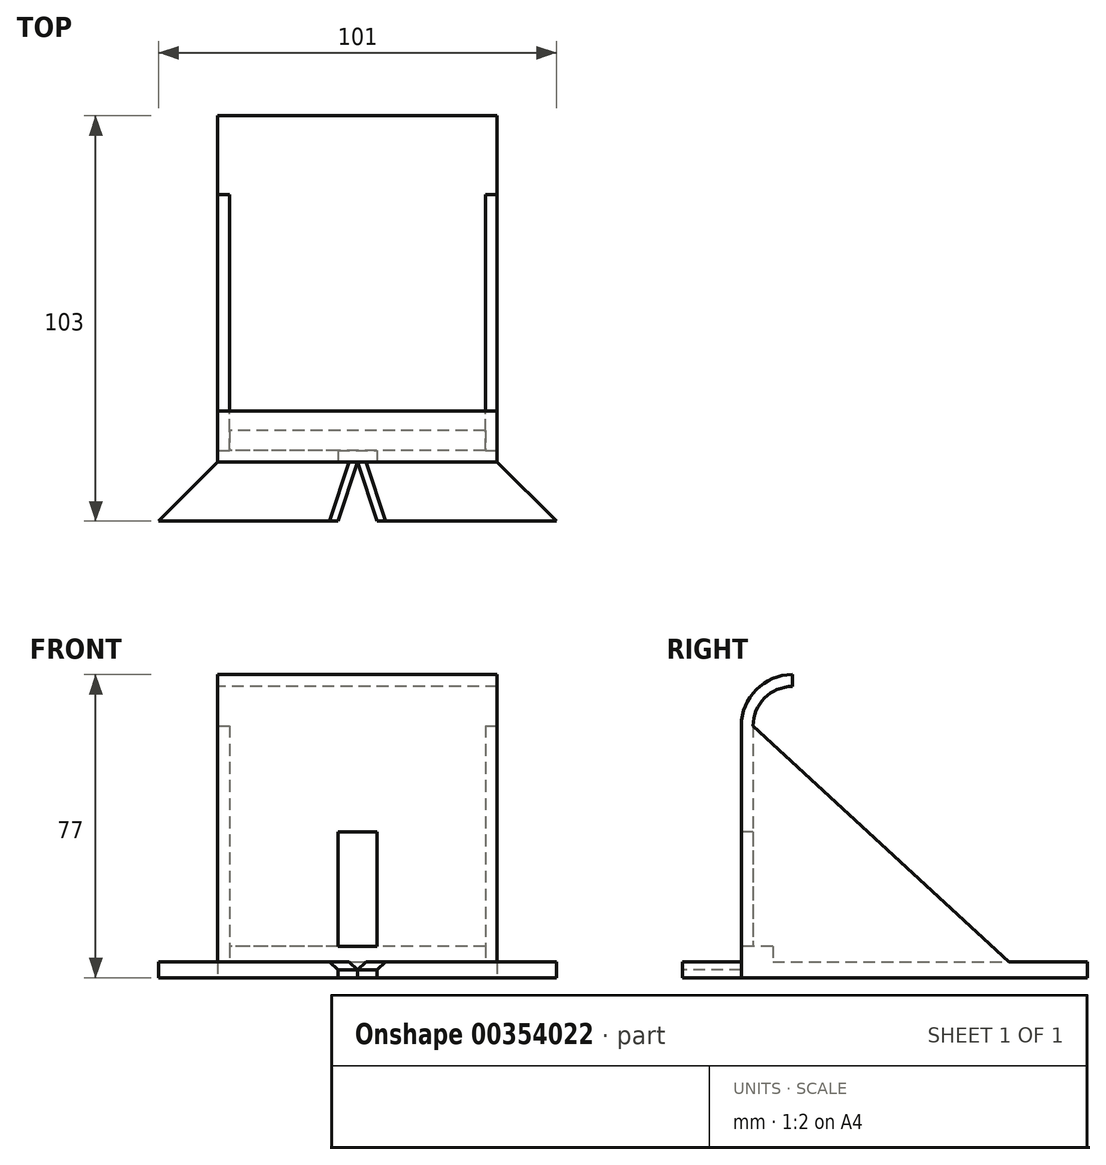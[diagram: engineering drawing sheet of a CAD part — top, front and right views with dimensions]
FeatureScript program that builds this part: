
annotation { "Feature Type Name" : "Feature", "Feature Type Description" : "" }
export const myFeature = defineFeature(function(context is Context, id is Id, definition is map)
    precondition{}
    {
        {
            var Q0;
            Q0=qCreatedBy(makeId("Top.planeOp"),FACE);
            var sketch = newSketch(context, id + "F0", { "sketchPlane" : qUnion([Q0])});
            skLineSegment(sketch, "E0.bottom", {"start": v(-32.5, -32.5) * mm, "end": v(32.5, -32.5) * mm});
            skLineSegment(sketch, "E0.top", {"start": v(-32.5, 32.5) * mm, "end": v(32.5, 32.5) * mm});
            skLineSegment(sketch, "E0.left", {"start": v(-32.5, -32.5) * mm, "end": v(-32.5, 32.5) * mm});
            skLineSegment(sketch, "E0.right", {"start": v(32.5, -32.5) * mm, "end": v(32.5, 32.5) * mm});
            skPoint(sketch, "E0.middle", {"position": v(0, 0) * mm});
            skLineSegment(sketch, "E1.0", {"start": v(35.5, -35.5) * mm, "end": v(35.5, 32.5) * mm});
            skLineSegment(sketch, "E1.1", {"start": v(-35.5, -35.5) * mm, "end": v(35.5, -35.5) * mm});
            skLineSegment(sketch, "E1.2", {"start": v(-35.5, -35.5) * mm, "end": v(-35.5, 32.5) * mm});
            skLineSegment(sketch, "E2", {"start": v(-32.5, 32.5) * mm, "end": v(-35.5, 32.5) * mm});
            skLineSegment(sketch, "E3", {"start": v(32.5, 32.5) * mm, "end": v(35.5, 32.5) * mm});
            skLineSegment(sketch, "E4", {"start": v(35.5, -35.5) * mm, "end": v(35.5, -50.5) * mm});
            skLineSegment(sketch, "E5", {"start": v(-35.5, -50.5) * mm, "end": v(-35.5, -35.5) * mm});
            skLineSegment(sketch, "E6", {"start": v(35.5, -35.5) * mm, "end": v(50.5, -50.5) * mm});
            skLineSegment(sketch, "E7.MirrorCS", {"start": v(-35.5, -35.5) * mm, "end": v(-50.5, -50.5) * mm});
            skLineSegment(sketch, "E8", {"start": v(5.98, -50.5) * mm, "end": v(5, -50.5) * mm});
            skLineSegment(sketch, "E9", {"start": v(5.98, -50.5) * mm, "end": v(50.5, -50.5) * mm});
            skLineSegment(sketch, "E10", {"start": v(5, -50.5) * mm, "end": v(0, -35.5) * mm});
            skLineSegment(sketch, "E11.MirrorCS", {"start": v(-5, -50.5) * mm, "end": v(0, -35.5) * mm});
            skLineSegment(sketch, "E12.trimOffspring", {"start": v(-5, -50.5) * mm, "end": v(-50.5, -50.5) * mm});
            skSolve(sketch);
        }
        {
            var Q0;
            Q0 = qSketchRegion(id + "F0", true);
            extrude(context, id + "F1", {"entities" : qUnion([Q0]), "depth" : 4 * mm});
        }
        {
            var Q0;
            Q0=makeQuery(id+"F1.opExtrude","CAP_FACE",FACE,{"disambiguationData":[OSD([sQuery(id+"F0.wireOp",EDGE,"E0.top"),sQuery(id+"F0.wireOp",EDGE,"E1.0"),sQuery(id+"F0.wireOp",EDGE,"E1.1"),sQuery(id+"F0.wireOp",EDGE,"E1.2"),sQuery(id+"F0.wireOp",EDGE,"E2"),sQuery(id+"F0.wireOp",EDGE,"E3")])],"isStart":false});
            var sketch = newSketch(context, id + "F2", { "sketchPlane" : qUnion([Q0])});
            skLineSegment(sketch, "E13.0", {"start": v(-32.5, -32.5) * mm, "end": v(32.5, -32.5) * mm});
            skLineSegment(sketch, "E14.0", {"start": v(-32.5, -32.5) * mm, "end": v(-32.5, 32.5) * mm});
            skLineSegment(sketch, "E15.0", {"start": v(32.5, -32.5) * mm, "end": v(32.5, 32.5) * mm});
            skLineSegment(sketch, "E16", {"start": v(-35.5, -35.5) * mm, "end": v(35.5, -35.5) * mm});
            skSolve(sketch);
        }
        {
            var Q0;
            Q0 = qSketchRegion(id + "F2", true);
            var Q1;
            Q1=makeQuery(id+"F2.imprint","IMPRINT",FACE,{"disambiguationData":[TD([[makeQuery(id+"F2.imprint","IMPRINT",EDGE,{"derivedFrom":sQuery(id+"F2.wireOp",EDGE,"E13.0")}),-1.0]])]});
            extrude(context, id + "F3", {"entities" : qUnion([Q0, Q1]), "operationType" : NewBodyOperationType.ADD, "depth" : 60 * mm});
        }
        {
            var Q0;
            {var subQ0=sQuery(id+"F0.wireOp",EDGE,"E1.0");Q0=makeQuery(id+"F3.boolean.opBoolean","MERGE",FACE,{"derivedFrom":[makeQuery(id+"F1.opExtrude","SWEPT_FACE",FACE,{"disambiguationData":[OSD([subQ0])]}),makeQuery(id+"F3.opExtrude","SWEPT_FACE",FACE,{"disambiguationData":[OSD([subQ0])]})]});}
            var sketch = newSketch(context, id + "F4", { "sketchPlane" : qUnion([Q0])});
            skLineSegment(sketch, "E17", {"start": v(32.5, 4) * mm, "end": v(-32.5, 64) * mm});
            skLineSegment(sketch, "E18.0.0", {"start": v(-35.5, 0) * mm, "end": v(32.5, 0) * mm});
            skLineSegment(sketch, "E18.0.1", {"start": v(32.5, 0) * mm, "end": v(32.5, 64) * mm});
            skLineSegment(sketch, "E18.0.2", {"start": v(32.5, 64) * mm, "end": v(-35.5, 64) * mm});
            skLineSegment(sketch, "E18.0.3", {"start": v(-35.5, 64) * mm, "end": v(-35.5, 0) * mm});
            skSolve(sketch);
        }
        {
            var Q0;
            {var subQ0=sQuery(id+"F4.wireOp",EDGE,"E17");Q0=makeQuery(id+"F4.imprint","IMPRINT",FACE,{"disambiguationData":[TD([[makeQuery(id+"F4.imprint","IMPRINT",EDGE,{"derivedFrom":subQ0}),-1.0]])]});}
            extrude(context, id + "F5", {"entities" : qUnion([Q0]), "operationType" : NewBodyOperationType.REMOVE, "oppositeDirection" : true, "depth" : 105.7 * mm});
        }
        {
            var Q0;
            Q0=makeQuery(id+"F3.opExtrude","SWEPT_FACE",FACE,{"disambiguationData":[OSD([sQuery(id+"F2.wireOp",EDGE,"E16")])]});
            var sketch = newSketch(context, id + "F6", { "sketchPlane" : qUnion([Q0])});
            skLineSegment(sketch, "E19", {"start": v(0, 8) * mm, "end": v(25, 8) * mm});
            skLineSegment(sketch, "E20", {"start": v(25, 8) * mm, "end": v(-25, 8) * mm});
            skLineSegment(sketch, "E21", {"start": v(-25, 8) * mm, "end": v(-25, 19) * mm});
            skLineSegment(sketch, "E22", {"start": v(0, 8) * mm, "end": v(3.48, 8) * mm});
            skLineSegment(sketch, "E23", {"start": v(0, 8) * mm, "end": v(-5, 8) * mm});
            skLineSegment(sketch, "E24", {"start": v(-5, 19) * mm, "end": v(-5, 37) * mm});
            skLineSegment(sketch, "E25", {"start": v(-25, 19) * mm, "end": v(-5, 19) * mm});
            skLineSegment(sketch, "E26", {"start": v(-5, 37) * mm, "end": v(0, 37) * mm});
            skPoint(sketch, "E26.endSnap0", {"position": v(0, 6) * mm});
            skLineSegment(sketch, "E27.MirrorCS", {"start": v(5, 19) * mm, "end": v(5, 37) * mm});
            skLineSegment(sketch, "E28.MirrorCS", {"start": v(5, 37) * mm, "end": v(0, 37) * mm});
            skLineSegment(sketch, "E29.MirrorCS", {"start": v(25, 19) * mm, "end": v(5, 19) * mm});
            skLineSegment(sketch, "E30.MirrorCS", {"start": v(25, 8) * mm, "end": v(25, 19) * mm});
            skPoint(sketch, "E31.orphan", {"position": v(5, 8) * mm});
            skSolve(sketch);
        }
        {
            var Q0;
            Q0 = qSketchRegion(id + "F6", true);
            extrude(context, id + "F7", {"entities" : qUnion([Q0]), "operationType" : NewBodyOperationType.REMOVE, "oppositeDirection" : true, "depth" : 25 * mm});
        }
        {
            var Q0;
            Q0=makeQuery(id+"F1.opExtrude","CAP_EDGE",EDGE,{"disambiguationData":[OSD([sQuery(id+"F0.wireOp",EDGE,"E11.MirrorCS")])],"isStart":false});
            chamfer(context, id + "F8", {"entities" : qUnion([Q0]), "width" : 2 * mm, "tangentPropagation" : true});
        }
        {
            var Q0;
            Q0=makeQuery(id+"F1.opExtrude","CAP_EDGE",EDGE,{"disambiguationData":[OSD([sQuery(id+"F0.wireOp",EDGE,"E10")])],"isStart":false});
            chamfer(context, id + "F9", {"entities" : qUnion([Q0]), "width" : 2 * mm, "tangentPropagation" : true});
        }
        {
            var Q0;
            {var subQ0=sQuery(id+"F0.wireOp",EDGE,"E3");var subQ1=sQuery(id+"F0.wireOp",EDGE,"E2");var subQ2=sQuery(id+"F0.wireOp",EDGE,"E0.top");var subQ3=makeQuery(id+"F1.opExtrude","CAP_EDGE",EDGE,{"disambiguationData":[OSD([subQ2,subQ1,subQ0])],"isStart":false});Q0=makeQuery(id+"F3.boolean.opBoolean","MERGE",FACE,{"derivedFrom":[makeQuery(id+"F1.opExtrude","SWEPT_FACE",FACE,{"disambiguationData":[OSD([subQ2,subQ1,subQ0])]}),makeQuery(id+"F3.opExtrude","SWEPT_FACE",FACE,{"disambiguationData":[OSD([subQ2,subQ1,subQ0]),TDD([makeQuery(id+"F2.imprint","IMPRINT",EDGE,{"disambiguationData":[TD([[makeQuery(id+"F2.imprint","INTERSECT",VERTEX,{"derivedFrom":[subQ3,makeQuery(id+"F1.opExtrude","CAP_EDGE",EDGE,{"disambiguationData":[OSD([sQuery(id+"F0.wireOp",EDGE,"E1.0")])],"isStart":false})]}),1.0]])],"derivedFrom":subQ3})])]}),makeQuery(id+"F3.opExtrude","SWEPT_FACE",FACE,{"disambiguationData":[OSD([subQ2,subQ1,subQ0]),TDD([makeQuery(id+"F2.imprint","IMPRINT",EDGE,{"disambiguationData":[TD([[makeQuery(id+"F2.imprint","INTERSECT",VERTEX,{"derivedFrom":[subQ3,makeQuery(id+"F1.opExtrude","CAP_EDGE",EDGE,{"disambiguationData":[OSD([sQuery(id+"F0.wireOp",EDGE,"E1.2")])],"isStart":false})]}),-1.0]])],"derivedFrom":subQ3})])]})]});}
            extrude(context, id + "F10", {"entities" : qUnion([Q0]), "operationType" : NewBodyOperationType.ADD, "depth" : 20 * mm});
        }
        {
            var Q0;
            Q0=makeQuery(id+"F7.boolean.opBoolean","COPY",FACE,{"derivedFrom":makeQuery(id+"F7.opExtrude","SWEPT_FACE",FACE,{"disambiguationData":[OSD([sQuery(id+"F6.wireOp",EDGE,"E29.MirrorCS")])]})});
            extrude(context, id + "F11", {"entities" : qUnion([Q0]), "operationType" : NewBodyOperationType.ADD, "oppositeDirection" : true, "depth" : 3 * mm});
        }
        {
            var Q0;
            Q0=makeQuery(id+"F7.boolean.opBoolean","COPY",FACE,{"derivedFrom":makeQuery(id+"F7.opExtrude","SWEPT_FACE",FACE,{"disambiguationData":[OSD([sQuery(id+"F6.wireOp",EDGE,"E25")])]})});
            extrude(context, id + "F12", {"entities" : qUnion([Q0]), "operationType" : NewBodyOperationType.ADD, "oppositeDirection" : true, "depth" : 3 * mm});
        }
        {
            var Q0;
            Q0=makeQuery(id+"F3.opExtrude","SWEPT_FACE",FACE,{"disambiguationData":[OSD([sQuery(id+"F2.wireOp",EDGE,"E13.0")])]});
            var sketch = newSketch(context, id + "F13", { "sketchPlane" : qUnion([Q0])});
            skLineSegment(sketch, "E32", {"start": v(25, 8) * mm, "end": v(32.5, 8) * mm});
            skLineSegment(sketch, "E33", {"start": v(-25, 8) * mm, "end": v(-32.5, 8) * mm});
            skSolve(sketch);
        }
        {
            var Q0;
            {var subQ5=sQuery(id+"F13.wireOp",EDGE,"E32");Q0=makeQuery(id+"F13.imprint","IMPRINT",FACE,{"disambiguationData":[TD([[makeQuery(id+"F13.imprint","IMPRINT",EDGE,{"derivedFrom":subQ5}),-1.0]])]});}
            extrude(context, id + "F14", {"entities" : qUnion([Q0]), "operationType" : NewBodyOperationType.ADD, "depth" : 5 * mm});
        }
        {
            var Q0;
            Q0=makeQuery(id+"F7.boolean.opBoolean","COPY",FACE,{"derivedFrom":makeQuery(id+"F7.opExtrude","SWEPT_FACE",FACE,{"disambiguationData":[OSD([sQuery(id+"F6.wireOp",EDGE,"E29.MirrorCS")])]})});
            extrude(context, id + "F15", {"entities" : qUnion([Q0]), "operationType" : NewBodyOperationType.ADD, "depth" : 15 * mm});
        }
        {
            var Q0;
            Q0=makeQuery(id+"F7.boolean.opBoolean","COPY",FACE,{"derivedFrom":makeQuery(id+"F7.opExtrude","SWEPT_FACE",FACE,{"disambiguationData":[OSD([sQuery(id+"F6.wireOp",EDGE,"E25")])]})});
            extrude(context, id + "F16", {"entities" : qUnion([Q0]), "operationType" : NewBodyOperationType.ADD, "depth" : 15 * mm});
        }
        {
            var Q0;
            {var subQ0=sQuery(id+"F0.wireOp",EDGE,"E1.2");Q0=makeQuery(id+"F10.boolean.opBoolean","MERGE",FACE,{"derivedFrom":[makeQuery(id+"F3.boolean.opBoolean","MERGE",FACE,{"derivedFrom":[makeQuery(id+"F1.opExtrude","SWEPT_FACE",FACE,{"disambiguationData":[OSD([subQ0])]}),makeQuery(id+"F3.opExtrude","SWEPT_FACE",FACE,{"disambiguationData":[OSD([subQ0])]})]}),makeQuery(id+"F10.opExtrude","SWEPT_FACE",FACE,{"disambiguationData":[OSD([sQuery(id+"F0.wireOp",EDGE,"E0.top"),subQ0,sQuery(id+"F0.wireOp",EDGE,"E2"),sQuery(id+"F0.wireOp",EDGE,"E3")])]})]});}
            var sketch = newSketch(context, id + "F17", { "sketchPlane" : qUnion([Q0])});
            skLineSegment(sketch, "E34", {"start": v(32.5, 64) * mm, "end": v(32.5, 74) * mm});
            skLineSegment(sketch, "E35", {"start": v(32.5, 74) * mm, "end": v(22.5, 74) * mm});
            skLineSegment(sketch, "E36", {"start": v(22.5, 74) * mm, "end": v(22.5, 77) * mm});
            skLineSegment(sketch, "E37", {"start": v(22.5, 77) * mm, "end": v(35.5, 77) * mm});
            skLineSegment(sketch, "E38", {"start": v(35.5, 77) * mm, "end": v(35.5, 64) * mm});
            skSolve(sketch);
        }
        {
            var Q0;
            Q0=makeQuery(id+"F17.imprint","IMPRINT",FACE,{"disambiguationData":[TD([[makeQuery(id+"F17.imprint","IMPRINT",EDGE,{"derivedFrom":sQuery(id+"F17.wireOp",EDGE,"E34")}),-1.0]])]});
            extrude(context, id + "F18", {"entities" : qUnion([Q0]), "operationType" : NewBodyOperationType.ADD, "oppositeDirection" : true, "depth" : 71 * mm});
        }
        {
            var Q0;
            Q0=makeQuery(id+"F18.opExtrude","SWEPT_EDGE",EDGE,{"disambiguationData":[OSD([sQuery(id+"F17.wireOp",EDGE,"E34"),sQuery(id+"F17.wireOp",EDGE,"E35")])]});
            fillet(context, id + "F19", {"entities" : qUnion([Q0]), "radius" : 10 * mm, "tangentPropagation" : true, "allowEdgeOverflow" : false});
        }
        {
            var Q0;
            Q0=makeQuery(id+"F18.opExtrude","SWEPT_EDGE",EDGE,{"disambiguationData":[OSD([sQuery(id+"F17.wireOp",EDGE,"E37"),sQuery(id+"F17.wireOp",EDGE,"E38")])]});
            fillet(context, id + "F20", {"entities" : qUnion([Q0]), "radius" : 13 * mm, "tangentPropagation" : true, "allowEdgeOverflow" : false});
        }
    });
